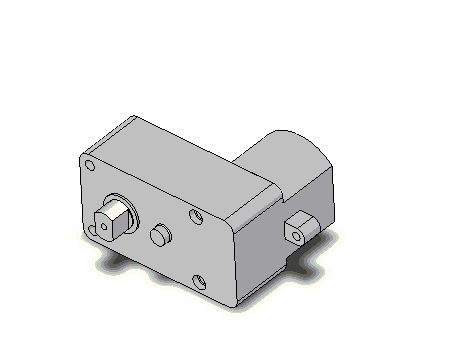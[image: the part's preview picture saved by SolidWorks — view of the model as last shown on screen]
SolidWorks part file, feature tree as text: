
SOLIDWORKS PART (.sldprt)
format: sldprt  version: not decoded by parser v0  size: 500,224 bytes
history: native  units: mm
features: sketch x16, extrude x8, plane x5, cut_extrude x5, chamfer x2, material x1, mirror x1 + 1 further entry (+13 scaffold rows collapsed)
feature tree (52):
  scaffold x13  (default folders/planes/origin — collapsed)
  material  "Material <not specified>"
  "Annotations"  RD1=4.445mm RD3=2mm RD2=2.286mm
  sketch  "Sketch1"  dims[c1.D3=2.5mm c1.D4=5.0mm c1.D6=2.5mm c1.D1=41.8mm c1.D2=22.7mm c2.D4=~40.298183mm c2.D5=21.2mm]
  extrude  "Base-Extrude"  Depth=15.8115mm
  sketch  "Sketch2"  dims[c1.D1=~4.28035mm c1.D2=9.271mm c1.D3=1.75mm c1.D4=3.5mm c2.D1=15.6mm c2.D4=~11.04392mm]
  extrude  "Boss-Extrude1"  Depth=0.55mm
  sketch  "Sketch3"  dims[D1=6.985mm D2=1.5mm]
  extrude  "Boss-Extrude2"  Depth=5.842mm
  plane  "Plane1"  Offset=5.08mm
  sketch  "Sketch5"  dims[D1=3.5mm D2=4.7752mm D3=2.3876mm]
  cut_extrude  "Cut-Extrude1"  [1 undecoded]
  sketch  "Sketch6"  dims[c1.D1=~1.372138mm c1.D2=3.937mm c2.D1=24.257mm]
  extrude  "Boss-Extrude3"  Depth=2mm
  plane  "Backside Plane"  Offset=0mm
  sketch  "Sketch8"
  plane  "Middle Plane"
  sketch  "Sketch11"  dims[c1.D1=7.2mm c1.D2=9.525mm c1.D3=6.9088mm c2.D1=~11.04392mm]
  extrude  "Boss-Extrude4"  Depth=2.794mm
  sketch  "Sketch12"  dims[D1=6.9088mm]
  extrude  "Boss-Extrude5"  Depth=6.731mm
  sketch  "Sketch15"  dims[c1.D2=~12.270569mm c1.D1=17.4mm c2.D1=15.66mm c2.D5=1.15mm c2.D6=1.0mm c2.D7=5.0mm]
  sketch  "Sketch16"  dims[c1.D1=~1.040407mm c1.D2=~0.973054mm c1.D5=2.0mm c2.D2=2.286mm c2.D1=2.0mm c2.D3=2.286mm c3.D1=5.334mm c3.D2=3.3mm c3.D3=4.572mm c3.D4=11.35mm c3.D5=11.35mm c4.D1=5.205mm c4.D2=3.3mm c4.D3=3.3mm c4.D4=3.3mm c5.D2=3.175mm]
  extrude  "Boss-Extrude7"  Depth=5.08mm
  sketch  "Sketch18"
  plane  "Plane5"
  mirror  "Mirror2"
  sketch  "Sketch33"
  sketch  "Sketch34"
  extrude  "Extrude1"  Depth=4.445mm
  sketch  "Sketch35"  dims[D1=6.096mm D2=11.35mm D3=7.55mm D4=7.55mm]
  cut_extrude  "Cut-Extrude4"  Depth=14.445mm
  cut_extrude  "Cut-Extrude5"  Depth=10mm
  chamfer  "Chamfer1"  Distance=0.25mm Angle=45deg
  chamfer  "Chamfer2"  Distance=0.25mm Angle=45deg
  sketch  "Sketch36"  dims[c1.D1=3.5mm c1.D2=3.5mm c2.D1=3.5mm c2.D2=~0.070127mm]
  cut_extrude  "Cut-Extrude6"  Depth=1.525mm
  plane  "Plane6"  Offset=4.191mm
  sketch  "Sketch38"  dims[c1.D2=6.9088mm c1.D1=4.699mm c2.D2=2.3495mm]
  cut_extrude  "Cut-Extrude7"  Depth=1.21mm Thickness=1.21mm
decode coverage: 26 of 32 modeling features carry decoded parameters; 1 rows unclassified (native names shown)
note: ~ marks probable driven/reference dimensions
note: 1 parameter value undecoded
note: suppression state not decoded; provenance and decode notes live in map.json
